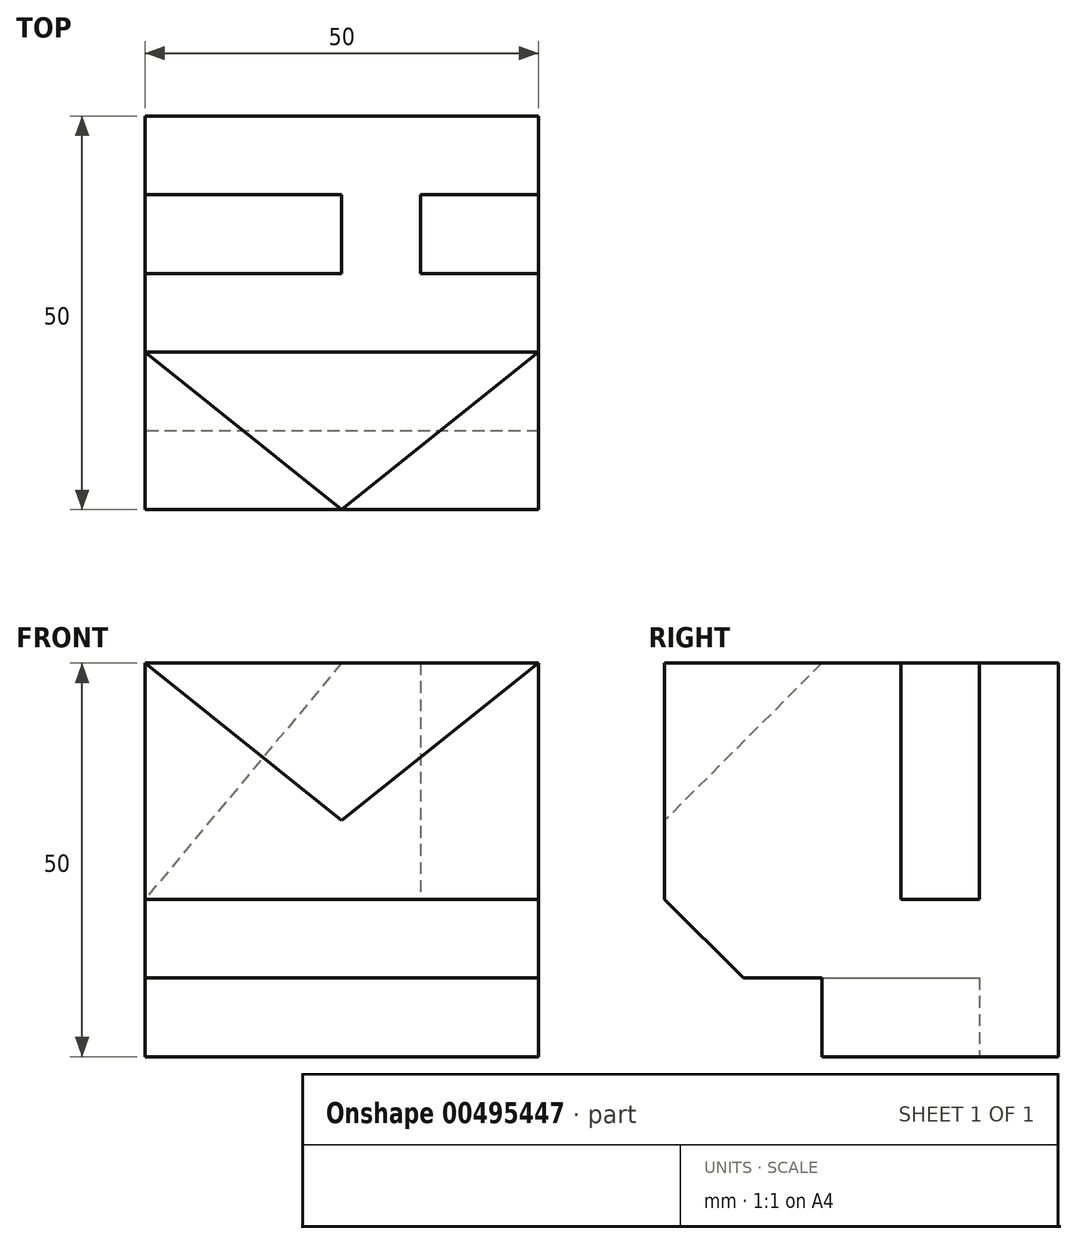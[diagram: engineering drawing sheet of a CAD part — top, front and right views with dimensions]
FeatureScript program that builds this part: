
annotation { "Feature Type Name" : "Feature", "Feature Type Description" : "" }
export const myFeature = defineFeature(function(context is Context, id is Id, definition is map)
    precondition{}
    {
        {
            var Q0;
            Q0=qCreatedBy(makeId("Top.planeOp"),FACE);
            var sketch = newSketch(context, id + "F0", { "sketchPlane" : qUnion([Q0])});
            skLineSegment(sketch, "E0.bottom", {"start": v(0, 0) * mm, "end": v(50, 0) * mm});
            skLineSegment(sketch, "E0.top", {"start": v(0, 50) * mm, "end": v(50, 50) * mm});
            skLineSegment(sketch, "E0.left", {"start": v(0, 0) * mm, "end": v(0, 50) * mm});
            skLineSegment(sketch, "E0.right", {"start": v(50, 0) * mm, "end": v(50, 50) * mm});
            skSolve(sketch);
        }
        {
            var Q0;
            Q0 = qSketchRegion(id + "F0", true);
            extrude(context, id + "F1", {"entities" : qUnion([Q0]), "depth" : 50 * mm});
        }
        {
            var Q0;
            Q0=makeQuery(id+"F1.opExtrude","SWEPT_FACE",FACE,{"disambiguationData":[OSD([sQuery(id+"F0.wireOp",EDGE,"E0.right")])]});
            var sketch = newSketch(context, id + "F2", { "sketchPlane" : qUnion([Q0])});
            skLineSegment(sketch, "E1.bottom", {"start": v(30, 50) * mm, "end": v(40, 50) * mm});
            skLineSegment(sketch, "E1.top", {"start": v(30, 20) * mm, "end": v(40, 20) * mm});
            skLineSegment(sketch, "E1.left", {"start": v(30, 50) * mm, "end": v(30, 20) * mm});
            skLineSegment(sketch, "E1.right", {"start": v(40, 50) * mm, "end": v(40, 20) * mm});
            skSolve(sketch);
        }
        {
            var Q0;
            Q0 = qSketchRegion(id + "F2", true);
            extrude(context, id + "F3", {"entities" : qUnion([Q0]), "operationType" : NewBodyOperationType.REMOVE, "oppositeDirection" : true, "depth" : 15 * mm});
        }
        {
            var Q0;
            Q0=makeQuery(id+"F1.opExtrude","CAP_FACE",FACE,{"disambiguationData":[OSD([sQuery(id+"F0.wireOp",EDGE,"E0.bottom"),sQuery(id+"F0.wireOp",EDGE,"E0.top"),sQuery(id+"F0.wireOp",EDGE,"E0.left"),sQuery(id+"F0.wireOp",EDGE,"E0.right")])],"isStart":false});
            var sketch = newSketch(context, id + "F4", { "sketchPlane" : qUnion([Q0])});
            skPoint(sketch, "E2", {"position": v(25, 40) * mm});
            skPoint(sketch, "E3", {"position": v(25, 30) * mm});
            skSolve(sketch);
        }
        {
            var Q0;
            Q0=makeQuery(id+"F1.opExtrude","SWEPT_FACE",FACE,{"disambiguationData":[OSD([sQuery(id+"F0.wireOp",EDGE,"E0.left")])]});
            var sketch = newSketch(context, id + "F5", { "sketchPlane" : qUnion([Q0])});
            skPoint(sketch, "E4", {"position": v(-35.39, 20) * mm});
            skSolve(sketch);
        }
        {
            var Q0;
            Q0=sQuery(id+"F4.wireOp",VERTEX,"E3");
            var Q1;
            Q1=sQuery(id+"F4.wireOp",VERTEX,"E2");
            var Q2;
            Q2=sQuery(id+"F5.wireOp",VERTEX,"E4");
            cPlane(context, id + "F6", {"entities" : qUnion([Q0, Q1, Q2]), "cplaneType" : CPlaneType.THREE_POINT, "offset" : 25 * mm, "width" : 150 * mm, "height" : 150 * mm});
        }
        {
            var Q0;
            {var subQ0=sQuery(id+"F0.wireOp",EDGE,"E0.left");Q0=makeQuery(id+"F5.imprint","IMPRINT",FACE,{"disambiguationData":[TD([[makeQuery(id+"F5.imprint","IMPRINT",EDGE,{"derivedFrom":makeQuery(id+"F1.opExtrude","CAP_EDGE",EDGE,{"disambiguationData":[OSD([subQ0])],"isStart":true})}),-1.0]])]});}
            var sketch = newSketch(context, id + "F7", { "sketchPlane" : qUnion([Q0])});
            skLineSegment(sketch, "E5.bottom", {"start": v(-40, 50) * mm, "end": v(-30, 50) * mm});
            skLineSegment(sketch, "E5.top", {"start": v(-40, 20) * mm, "end": v(-30, 20) * mm});
            skLineSegment(sketch, "E5.left", {"start": v(-40, 50) * mm, "end": v(-40, 20) * mm});
            skLineSegment(sketch, "E5.right", {"start": v(-30, 50) * mm, "end": v(-30, 20) * mm});
            skSolve(sketch);
        }
        {
            var Q0;
            Q0 = qSketchRegion(id + "F7", true);
            var Q1;
            Q1=qCreatedBy(id+"F6.planeOp",FACE);
            extrude(context, id + "F8", {"entities" : qUnion([Q0]), "operationType" : NewBodyOperationType.REMOVE, "endBound" : BoundingType.UP_TO_SURFACE, "oppositeDirection" : true, "endBoundEntityFace" : qUnion([Q1]), "depth" : 25 * mm});
        }
        {
            var Q0;
            {var subQ0=sQuery(id+"F0.wireOp",EDGE,"E0.left");Q0=makeQuery(id+"F5.imprint","IMPRINT",FACE,{"disambiguationData":[TD([[makeQuery(id+"F5.imprint","IMPRINT",EDGE,{"derivedFrom":makeQuery(id+"F1.opExtrude","CAP_EDGE",EDGE,{"disambiguationData":[OSD([subQ0])],"isStart":true})}),-1.0]])]});}
            var sketch = newSketch(context, id + "F9", { "sketchPlane" : qUnion([Q0])});
            skLineSegment(sketch, "E6.bottom", {"start": v(0, 0) * mm, "end": v(-20, 0) * mm});
            skLineSegment(sketch, "E6.top", {"start": v(0, 10) * mm, "end": v(-20, 10) * mm});
            skLineSegment(sketch, "E6.left", {"start": v(0, 0) * mm, "end": v(0, 10) * mm});
            skLineSegment(sketch, "E6.right", {"start": v(-20, 0) * mm, "end": v(-20, 10) * mm});
            skSolve(sketch);
        }
        {
            var Q0;
            Q0 = qSketchRegion(id + "F9", true);
            extrude(context, id + "F10", {"entities" : qUnion([Q0]), "operationType" : NewBodyOperationType.REMOVE, "endBound" : BoundingType.THROUGH_ALL, "oppositeDirection" : true, "depth" : 25 * mm});
        }
        {
            var Q0;
            {var subQ0=sQuery(id+"F0.wireOp",EDGE,"E0.left");Q0=makeQuery(id+"F5.imprint","IMPRINT",FACE,{"disambiguationData":[TD([[makeQuery(id+"F5.imprint","IMPRINT",EDGE,{"derivedFrom":makeQuery(id+"F1.opExtrude","CAP_EDGE",EDGE,{"disambiguationData":[OSD([subQ0])],"isStart":true})}),-1.0]])]});}
            var sketch = newSketch(context, id + "F11", { "sketchPlane" : qUnion([Q0])});
            skLineSegment(sketch, "E7", {"start": v(0, 20) * mm, "end": v(-10, 10) * mm});
            skLineSegment(sketch, "E8", {"start": v(-10, 10) * mm, "end": v(0, 10) * mm});
            skLineSegment(sketch, "E9", {"start": v(0, 10) * mm, "end": v(0, 20) * mm});
            skSolve(sketch);
        }
        {
            var Q0;
            Q0 = qSketchRegion(id + "F11", true);
            extrude(context, id + "F12", {"entities" : qUnion([Q0]), "operationType" : NewBodyOperationType.REMOVE, "endBound" : BoundingType.UP_TO_NEXT, "oppositeDirection" : true, "depth" : 25 * mm});
        }
        {
            var Q0;
            Q0=makeQuery(id+"F1.opExtrude","SWEPT_FACE",FACE,{"disambiguationData":[OSD([sQuery(id+"F0.wireOp",EDGE,"E0.bottom")])]});
            var sketch = newSketch(context, id + "F13", { "sketchPlane" : qUnion([Q0])});
            skPoint(sketch, "E10", {"position": v(25, 30) * mm});
            skSolve(sketch);
        }
        {
            var Q0;
            {var subQ0=sQuery(id+"F0.wireOp",EDGE,"E0.bottom");Q0=makeQuery(id+"F13.imprint","IMPRINT",FACE,{"disambiguationData":[TD([[makeQuery(id+"F13.imprint","IMPRINT",EDGE,{"derivedFrom":makeQuery(id+"F1.opExtrude","CAP_EDGE",EDGE,{"disambiguationData":[OSD([subQ0])],"isStart":false})}),-1.0]])]});}
            var sketch = newSketch(context, id + "F14", { "sketchPlane" : qUnion([Q0])});
            skPoint(sketch, "E11", {"position": v(25, 50) * mm});
            skSolve(sketch);
        }
        {
            var Q0;
            {var subQ0=sQuery(id+"F0.wireOp",EDGE,"E0.bottom");Q0=makeQuery(id+"F13.imprint","IMPRINT",FACE,{"disambiguationData":[TD([[makeQuery(id+"F13.imprint","IMPRINT",EDGE,{"derivedFrom":makeQuery(id+"F1.opExtrude","CAP_EDGE",EDGE,{"disambiguationData":[OSD([subQ0])],"isStart":false})}),-1.0]])]});}
            var sketch = newSketch(context, id + "F15", { "sketchPlane" : qUnion([Q0])});
            skLineSegment(sketch, "E12", {"start": v(0, 50) * mm, "end": v(50, 50) * mm});
            skLineSegment(sketch, "E13", {"start": v(50, 50) * mm, "end": v(25, 30) * mm});
            skLineSegment(sketch, "E14", {"start": v(25, 30) * mm, "end": v(0, 50) * mm});
            skSolve(sketch);
        }
        {
            var Q0;
            {var subQ5=sQuery(id+"F0.wireOp",EDGE,"E0.bottom");Q0=makeQuery(id+"F4.imprint","IMPRINT",FACE,{"disambiguationData":[TD([[makeQuery(id+"F4.imprint","IMPRINT",EDGE,{"derivedFrom":makeQuery(id+"F1.opExtrude","CAP_EDGE",EDGE,{"disambiguationData":[OSD([subQ5])],"isStart":false})}),1.0]])]});}
            var sketch = newSketch(context, id + "F16", { "sketchPlane" : qUnion([Q0])});
            skPoint(sketch, "E15", {"position": v(0, 20) * mm});
            skPoint(sketch, "E16", {"position": v(50, 20) * mm});
            skSolve(sketch);
        }
        {
            var Q0;
            Q0=sQuery(id+"F16.wireOp",VERTEX,"E15");
            var Q1;
            Q1=sQuery(id+"F16.wireOp",VERTEX,"E16");
            var Q2;
            Q2=sQuery(id+"F13.wireOp",VERTEX,"E10");
            cPlane(context, id + "F17", {"entities" : qUnion([Q0, Q1, Q2]), "cplaneType" : CPlaneType.THREE_POINT, "offset" : 25 * mm, "width" : 150 * mm, "height" : 150 * mm});
        }
        {
            var Q0;
            Q0=makeQuery(id+"F15.imprint","IMPRINT",FACE,{"disambiguationData":[TD([[makeQuery(id+"F15.imprint","IMPRINT",EDGE,{"derivedFrom":sQuery(id+"F15.wireOp",EDGE,"E12")}),-1.0]])]});
            var Q1;
            Q1=qCreatedBy(id+"F17.planeOp",FACE);
            extrude(context, id + "F18", {"entities" : qUnion([Q0]), "operationType" : NewBodyOperationType.REMOVE, "endBound" : BoundingType.UP_TO_SURFACE, "oppositeDirection" : true, "depth" : 25 * mm, "endBoundEntityFace" : qUnion([Q1]), "offsetDistance" : 25 * mm});
        }
        {
            var Q0;
            Q0=makeQuery(id+"F1.opExtrude","CAP_FACE",FACE,{"disambiguationData":[OSD([sQuery(id+"F0.wireOp",EDGE,"E0.bottom"),sQuery(id+"F0.wireOp",EDGE,"E0.top"),sQuery(id+"F0.wireOp",EDGE,"E0.left"),sQuery(id+"F0.wireOp",EDGE,"E0.right")])],"isStart":true});
            var sketch = newSketch(context, id + "F19", { "sketchPlane" : qUnion([Q0])});
            skLineSegment(sketch, "E17", {"start": v(0, -20) * mm, "end": v(50, -20) * mm});
            skLineSegment(sketch, "E18", {"start": v(50, -20) * mm, "end": v(0, -40) * mm});
            skLineSegment(sketch, "E19", {"start": v(0, -40) * mm, "end": v(0, -20) * mm});
            skSolve(sketch);
        }
        {
            var Q0;
            Q0 = qSketchRegion(id + "F19", true);
            extrude(context, id + "F20", {"entities" : qUnion([Q0]), "operationType" : NewBodyOperationType.REMOVE, "oppositeDirection" : true, "depth" : 10 * mm, "offsetDistance" : 25 * mm});
        }
    });
